# Revit family: IS_IdealrainCube_B0002_BIM_GB
name_source: partatom
category: Plumbing Fixtures
revit_build: Autodesk Revit MEP 2014 (Build: 20130308_1515(x64)
units: mm (PartAtom-declared; Revit-internal decimal feet)

## types (1)
- B0002AA - Idealrain Cube M1 Shower Handspray - 100mm - Single Funtion
    Accessories = www.idealspec.co.uk
    AreaUnits = millimeters
    Assembly Code = C1030200
    AssetType = Fixed
    BIMObjectName = ISI_IdealStandard_ShowerMixers_IdealRain_B0002AA
    BREEAMApproved = No
    BarCode = 3800861033691
    Brand = Ideal Standard
    CWFU = 0
    Color = Chrome
    ConnectionType = Plumbing
    Cost = 0 $
    Default Elevation = 800 mm
    Description = Idealrain Cube M1 shower handspray, single function 100mm
    DurationUnit = year
    ECA = No
    ExpectedLife = 30
    FaucetFunction = MIXED
    FaucetOperation = LEVERHANDLE
    Features = M1 shower handspray, single function 100mm
    Finish = Chrome
    FlowRate = 8L/min @ 3bar
    HWFU = 0
    Help = www.idealspec.co.uk/contact-us.html
    IfcExportAs = IfcValveType
    IfcExportType = SHOWERS
    InstallationInstructions = www.idealspec.co.uk/resources.html
    LinearUnits = millimeters
    ManufacturerURL = www.idealspec.co.uk
    Material = Brass
    MetalMtl = ISI_IdealStandard_Brassware_Chrome_Render
    Model = B0002AA
    NBSDescription = Shower head
    NBSReference = 45-35-70/333
    Name = ShowerMixers_IdealRain_A5691AA_IdealStandard
    NettWeight = 0.3Kg
    NominalHeight = 0 mm  [stored 0 ft]
    NominalLength = 245 mm  [stored 0.803806 ft]
    NominalWidth = 100 mm  [stored 0.328084 ft]
    PlasticMtl = ISI_IdealStandard_Brassware_Plastic_Render
    ProductInformation = www.idealspec.co.uk/assets/datasheet/B0002AA
    Shape = Sculptured
    Size = 0 x 245 x 100 mm
    Space = Internal
    SpareParts = www.fastpart-spares.co.uk
    TMV3 = Yes
    TestPressure = 10 Bar
    URL = www.idealspec.co.uk
    Uniclass2015Code = Pr_40_20_87_76
    Uniclass2015Title = Shower head
    Uniclass2015Version = Product v1.1
    Version = 1
    VolumeUnits = Litres
    WFU = 0
    WRAS = Yes
    WarrantyDescription = Manufacturers Warranty
    WarrantyDurationParts = 5
    WarrantyDurationUnit = year
    WaterEfficientProduct = No
    WorkingPressure = 3 Bar

note: [stored X ft] marks values corroborated as IEEE doubles in the binary element streams (Revit-internal decimal feet)

## geometry (parser evidence)
native form markers: Sweep x3
no freeform markers — native parametric forms only
